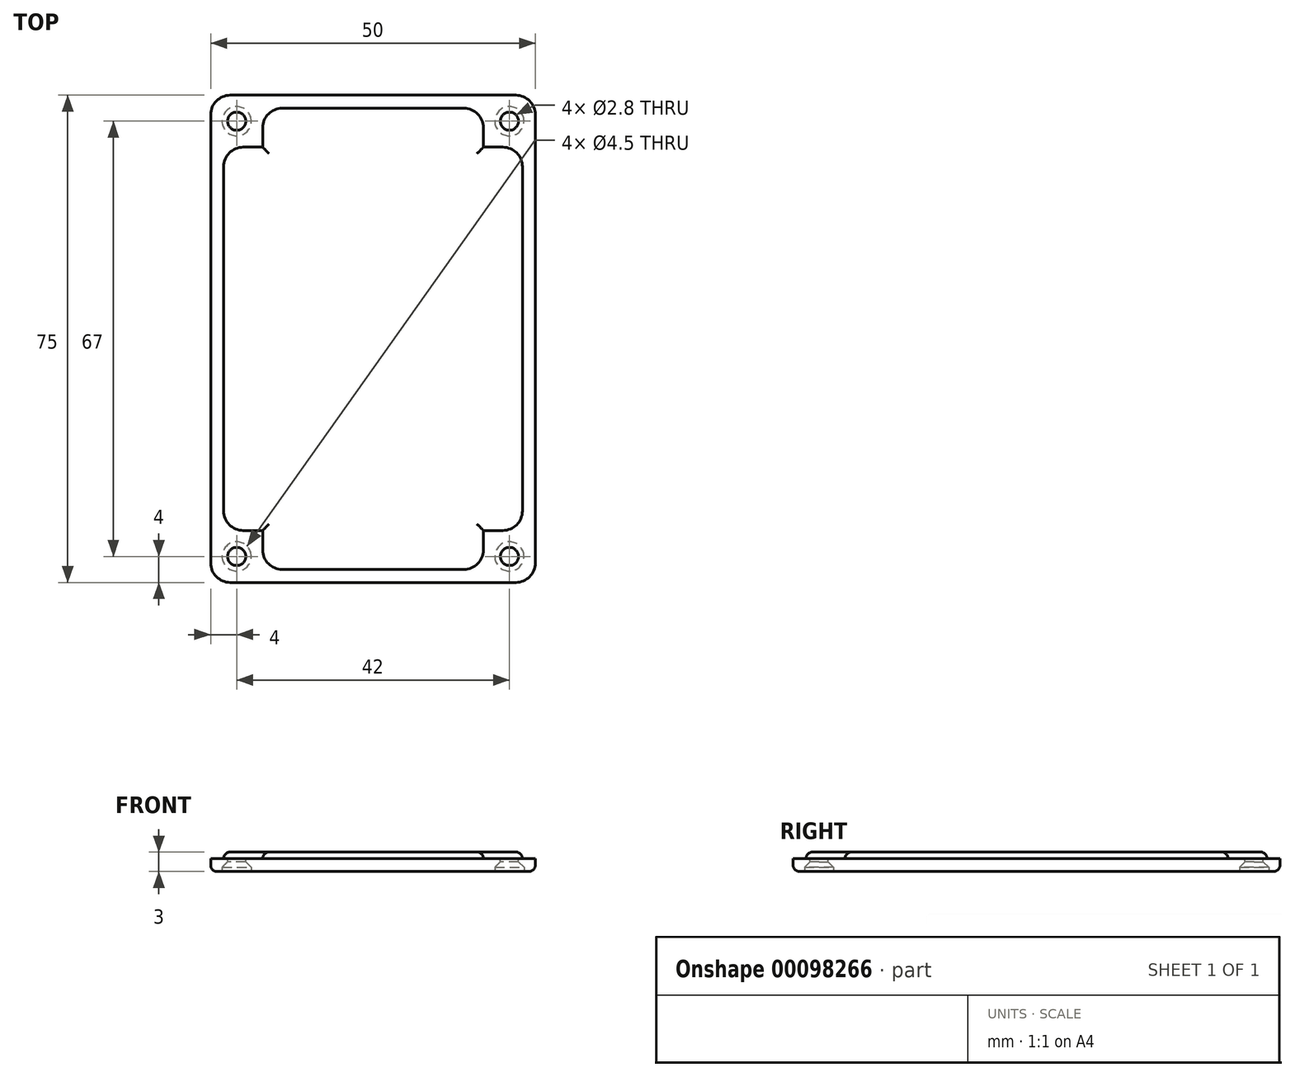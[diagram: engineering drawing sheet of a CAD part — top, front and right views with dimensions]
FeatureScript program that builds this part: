
annotation { "Feature Type Name" : "Feature", "Feature Type Description" : "" }
export const myFeature = defineFeature(function(context is Context, id is Id, definition is map)
    precondition{}
    {
        {
            var Q0;
            Q0=qCreatedBy(makeId("Top.planeOp"),FACE);
            var sketch = newSketch(context, id + "F0", { "sketchPlane" : qUnion([Q0])});
            skLineSegment(sketch, "E0.bottom", {"start": v(3, 0) * mm, "end": v(47, 0) * mm});
            skLineSegment(sketch, "E0.top", {"start": v(3, 75) * mm, "end": v(47, 75) * mm});
            skLineSegment(sketch, "E0.left", {"start": v(0, 3) * mm, "end": v(0, 72) * mm});
            skLineSegment(sketch, "E0.right", {"start": v(50, 3) * mm, "end": v(50, 72) * mm});
            skPoint(sketch, "E1.visualSharp", {"position": v(0, 75) * mm});
            skArc(sketch, "E1.filletArc", {"start": v(3, 75) * mm, "mid": v(0.88, 74.12) * mm, "end": v(0, 72) * mm});
            skPoint(sketch, "E2.visualSharp", {"position": v(50, 75) * mm});
            skArc(sketch, "E2.filletArc", {"start": v(50, 72) * mm, "mid": v(49.12, 74.12) * mm, "end": v(47, 75) * mm});
            skPoint(sketch, "E3.visualSharp", {"position": v(50, 0) * mm});
            skArc(sketch, "E3.filletArc", {"start": v(47, 0) * mm, "mid": v(49.12, 0.88) * mm, "end": v(50, 3) * mm});
            skPoint(sketch, "E4.visualSharp", {"position": v(0, 0) * mm});
            skArc(sketch, "E4.filletArc", {"start": v(0, 3) * mm, "mid": v(0.88, 0.88) * mm, "end": v(3, 0) * mm});
            skSolve(sketch);
        }
        {
            var Q0;
            Q0=makeQuery(id+"F0.imprint","IMPRINT",FACE,{"disambiguationData":[TD([[makeQuery(id+"F0.imprint","IMPRINT",EDGE,{"derivedFrom":sQuery(id+"F0.wireOp",EDGE,"E0.bottom")}),1.0]])]});
            extrude(context, id + "F1", {"entities" : qUnion([Q0]), "depth" : 2 * mm});
        }
        {
            var Q0;
            Q0=makeQuery(id+"F1.opExtrude","CAP_FACE",FACE,{"disambiguationData":[OSD([sQuery(id+"F0.wireOp",EDGE,"E0.bottom"),sQuery(id+"F0.wireOp",EDGE,"E0.top"),sQuery(id+"F0.wireOp",EDGE,"E0.left"),sQuery(id+"F0.wireOp",EDGE,"E0.right"),sQuery(id+"F0.wireOp",EDGE,"E1.filletArc"),sQuery(id+"F0.wireOp",EDGE,"E2.filletArc"),sQuery(id+"F0.wireOp",EDGE,"E3.filletArc"),sQuery(id+"F0.wireOp",EDGE,"E4.filletArc")])],"isStart":false});
            var sketch = newSketch(context, id + "F2", { "sketchPlane" : qUnion([Q0])});
            skCircle(sketch, "E5", {"center": v(4, 71) * mm, "radius": 1.4 * mm});
            skCircle(sketch, "E6", {"center": v(46, 71) * mm, "radius": 1.4 * mm});
            skCircle(sketch, "E7", {"center": v(46, 4) * mm, "radius": 1.4 * mm});
            skCircle(sketch, "E8", {"center": v(4, 4) * mm, "radius": 1.4 * mm});
            skSolve(sketch);
        }
        {
            var Q0;
            Q0=makeQuery(id+"F2.imprint","IMPRINT",FACE,{"disambiguationData":[TD([[makeQuery(id+"F2.imprint","IMPRINT",EDGE,{"derivedFrom":sQuery(id+"F2.wireOp",EDGE,"E5")}),1.0]])]});
            var Q1;
            Q1=makeQuery(id+"F2.imprint","IMPRINT",FACE,{"disambiguationData":[TD([[makeQuery(id+"F2.imprint","IMPRINT",EDGE,{"derivedFrom":sQuery(id+"F2.wireOp",EDGE,"E6")}),1.0]])]});
            var Q2;
            Q2=makeQuery(id+"F2.imprint","IMPRINT",FACE,{"disambiguationData":[TD([[makeQuery(id+"F2.imprint","IMPRINT",EDGE,{"derivedFrom":sQuery(id+"F2.wireOp",EDGE,"E8")}),1.0]])]});
            var Q3;
            Q3=makeQuery(id+"F2.imprint","IMPRINT",FACE,{"disambiguationData":[TD([[makeQuery(id+"F2.imprint","IMPRINT",EDGE,{"derivedFrom":sQuery(id+"F2.wireOp",EDGE,"E7")}),1.0]])]});
            extrude(context, id + "F3", {"entities" : qUnion([Q0, Q1, Q2, Q3]), "operationType" : NewBodyOperationType.REMOVE, "oppositeDirection" : true, "depth" : 5 * mm});
        }
        {
            var Q0;
            Q0=makeQuery(id+"F1.opExtrude","CAP_FACE",FACE,{"disambiguationData":[OSD([sQuery(id+"F0.wireOp",EDGE,"E0.bottom"),sQuery(id+"F0.wireOp",EDGE,"E0.top"),sQuery(id+"F0.wireOp",EDGE,"E0.left"),sQuery(id+"F0.wireOp",EDGE,"E0.right"),sQuery(id+"F0.wireOp",EDGE,"E1.filletArc"),sQuery(id+"F0.wireOp",EDGE,"E2.filletArc"),sQuery(id+"F0.wireOp",EDGE,"E3.filletArc"),sQuery(id+"F0.wireOp",EDGE,"E4.filletArc")])],"isStart":false});
            var sketch = newSketch(context, id + "F4", { "sketchPlane" : qUnion([Q0])});
            skLineSegment(sketch, "E9.1", {"start": v(11, 2) * mm, "end": v(39, 2) * mm});
            skLineSegment(sketch, "E9.2", {"start": v(2, 11) * mm, "end": v(2, 64) * mm});
            skLineSegment(sketch, "E9.5", {"start": v(11, 73) * mm, "end": v(39, 73) * mm});
            skLineSegment(sketch, "E9.7", {"start": v(48, 11) * mm, "end": v(48, 64) * mm});
            skLineSegment(sketch, "E10.top", {"start": v(5, 67) * mm, "end": v(8, 67) * mm});
            skLineSegment(sketch, "E10.right", {"start": v(8, 70) * mm, "end": v(8, 67) * mm});
            skLineSegment(sketch, "E11.top", {"start": v(45, 67) * mm, "end": v(42, 67) * mm});
            skLineSegment(sketch, "E11.right", {"start": v(42, 70) * mm, "end": v(42, 67) * mm});
            skLineSegment(sketch, "E12.top", {"start": v(45, 8) * mm, "end": v(42, 8) * mm});
            skLineSegment(sketch, "E12.right", {"start": v(42, 5) * mm, "end": v(42, 8) * mm});
            skLineSegment(sketch, "E13.top", {"start": v(5, 8) * mm, "end": v(8, 8) * mm});
            skLineSegment(sketch, "E13.right", {"start": v(8, 5) * mm, "end": v(8, 8) * mm});
            skPoint(sketch, "E14.visualSharp", {"position": v(2, 67) * mm});
            skArc(sketch, "E14.filletArc", {"start": v(5, 67) * mm, "mid": v(2.88, 66.12) * mm, "end": v(2, 64) * mm});
            skPoint(sketch, "E15.visualSharp", {"position": v(8, 73) * mm});
            skArc(sketch, "E15.filletArc", {"start": v(11, 73) * mm, "mid": v(8.88, 72.12) * mm, "end": v(8, 70) * mm});
            skPoint(sketch, "E16.visualSharp", {"position": v(42, 73) * mm});
            skArc(sketch, "E16.filletArc", {"start": v(42, 70) * mm, "mid": v(41.12, 72.12) * mm, "end": v(39, 73) * mm});
            skPoint(sketch, "E17.visualSharp", {"position": v(48, 67) * mm});
            skArc(sketch, "E17.filletArc", {"start": v(48, 64) * mm, "mid": v(47.12, 66.12) * mm, "end": v(45, 67) * mm});
            skPoint(sketch, "E18.visualSharp", {"position": v(48, 8) * mm});
            skArc(sketch, "E18.filletArc", {"start": v(45, 8) * mm, "mid": v(47.12, 8.88) * mm, "end": v(48, 11) * mm});
            skPoint(sketch, "E19.visualSharp", {"position": v(42, 2) * mm});
            skArc(sketch, "E19.filletArc", {"start": v(39, 2) * mm, "mid": v(41.12, 2.88) * mm, "end": v(42, 5) * mm});
            skPoint(sketch, "E20.visualSharp", {"position": v(8, 2) * mm});
            skArc(sketch, "E20.filletArc", {"start": v(8, 5) * mm, "mid": v(8.88, 2.88) * mm, "end": v(11, 2) * mm});
            skPoint(sketch, "E21.visualSharp", {"position": v(2, 8) * mm});
            skArc(sketch, "E21.filletArc", {"start": v(2, 11) * mm, "mid": v(2.88, 8.88) * mm, "end": v(5, 8) * mm});
            skSolve(sketch);
        }
        {
            var Q0;
            Q0=makeQuery(id+"F4.imprint","IMPRINT",FACE,{"disambiguationData":[TD([[makeQuery(id+"F4.imprint","IMPRINT",EDGE,{"derivedFrom":sQuery(id+"F4.wireOp",EDGE,"E9.1")}),1.0]])]});
            extrude(context, id + "F5", {"entities" : qUnion([Q0]), "operationType" : NewBodyOperationType.ADD, "depth" : 1 * mm});
        }
        {
            var Q0;
            Q0=makeQuery(id+"F5.opExtrude","CAP_EDGE",EDGE,{"disambiguationData":[OSD([sQuery(id+"F4.wireOp",EDGE,"E18.filletArc")])],"isStart":false});
            var Q1;
            Q1=makeQuery(id+"F5.opExtrude","CAP_EDGE",EDGE,{"disambiguationData":[OSD([sQuery(id+"F4.wireOp",EDGE,"E12.top")])],"isStart":false});
            var Q2;
            Q2=makeQuery(id+"F5.opExtrude","CAP_EDGE",EDGE,{"disambiguationData":[OSD([sQuery(id+"F4.wireOp",EDGE,"E12.right")])],"isStart":false});
            var Q3;
            Q3=makeQuery(id+"F5.opExtrude","CAP_EDGE",EDGE,{"disambiguationData":[OSD([sQuery(id+"F4.wireOp",EDGE,"E19.filletArc")])],"isStart":false});
            var Q4;
            Q4=makeQuery(id+"F5.opExtrude","CAP_EDGE",EDGE,{"disambiguationData":[OSD([sQuery(id+"F4.wireOp",EDGE,"E9.1")])],"isStart":false});
            var Q5;
            Q5=makeQuery(id+"F5.opExtrude","CAP_EDGE",EDGE,{"disambiguationData":[OSD([sQuery(id+"F4.wireOp",EDGE,"E20.filletArc")])],"isStart":false});
            var Q6;
            Q6=makeQuery(id+"F5.opExtrude","CAP_EDGE",EDGE,{"disambiguationData":[OSD([sQuery(id+"F4.wireOp",EDGE,"E13.right")])],"isStart":false});
            var Q7;
            Q7=makeQuery(id+"F5.opExtrude","CAP_EDGE",EDGE,{"disambiguationData":[OSD([sQuery(id+"F4.wireOp",EDGE,"E13.top")])],"isStart":false});
            var Q8;
            Q8=makeQuery(id+"F5.opExtrude","CAP_EDGE",EDGE,{"disambiguationData":[OSD([sQuery(id+"F4.wireOp",EDGE,"E21.filletArc")])],"isStart":false});
            var Q9;
            Q9=makeQuery(id+"F5.opExtrude","CAP_EDGE",EDGE,{"disambiguationData":[OSD([sQuery(id+"F4.wireOp",EDGE,"E9.2")])],"isStart":false});
            var Q10;
            Q10=makeQuery(id+"F5.opExtrude","CAP_EDGE",EDGE,{"disambiguationData":[OSD([sQuery(id+"F4.wireOp",EDGE,"E14.filletArc")])],"isStart":false});
            var Q11;
            Q11=makeQuery(id+"F5.opExtrude","CAP_EDGE",EDGE,{"disambiguationData":[OSD([sQuery(id+"F4.wireOp",EDGE,"E10.top")])],"isStart":false});
            var Q12;
            Q12=makeQuery(id+"F5.opExtrude","CAP_EDGE",EDGE,{"disambiguationData":[OSD([sQuery(id+"F4.wireOp",EDGE,"E10.right")])],"isStart":false});
            var Q13;
            Q13=makeQuery(id+"F5.opExtrude","CAP_EDGE",EDGE,{"disambiguationData":[OSD([sQuery(id+"F4.wireOp",EDGE,"E15.filletArc")])],"isStart":false});
            var Q14;
            Q14=makeQuery(id+"F5.opExtrude","CAP_EDGE",EDGE,{"disambiguationData":[OSD([sQuery(id+"F4.wireOp",EDGE,"E9.5")])],"isStart":false});
            var Q15;
            Q15=makeQuery(id+"F5.opExtrude","CAP_EDGE",EDGE,{"disambiguationData":[OSD([sQuery(id+"F4.wireOp",EDGE,"E16.filletArc")])],"isStart":false});
            var Q16;
            Q16=makeQuery(id+"F5.opExtrude","CAP_EDGE",EDGE,{"disambiguationData":[OSD([sQuery(id+"F4.wireOp",EDGE,"E11.right")])],"isStart":false});
            var Q17;
            Q17=makeQuery(id+"F5.opExtrude","CAP_EDGE",EDGE,{"disambiguationData":[OSD([sQuery(id+"F4.wireOp",EDGE,"E11.top")])],"isStart":false});
            var Q18;
            Q18=makeQuery(id+"F5.opExtrude","CAP_EDGE",EDGE,{"disambiguationData":[OSD([sQuery(id+"F4.wireOp",EDGE,"E17.filletArc")])],"isStart":false});
            var Q19;
            Q19=makeQuery(id+"F5.opExtrude","CAP_EDGE",EDGE,{"disambiguationData":[OSD([sQuery(id+"F4.wireOp",EDGE,"E9.7")])],"isStart":false});
            fillet(context, id + "F6", {"entities" : qUnion([Q0, Q1, Q2, Q3, Q4, Q5, Q6, Q7, Q8, Q9, Q10, Q11, Q12, Q13, Q14, Q15, Q16, Q17, Q18, Q19]), "radius" : 1 * mm, "tangentPropagation" : true, "allowEdgeOverflow" : false});
        }
        {
            var Q0;
            Q0=makeQuery(id+"F1.opExtrude","CAP_EDGE",EDGE,{"disambiguationData":[OSD([sQuery(id+"F0.wireOp",EDGE,"E0.left")])],"isStart":true});
            fillet(context, id + "F7", {"entities" : qUnion([Q0]), "radius" : 1 * mm, "tangentPropagation" : true, "allowEdgeOverflow" : false});
        }
        {
            var Q0;
            Q0=makeQuery(id+"F1.opExtrude","CAP_FACE",FACE,{"disambiguationData":[OSD([sQuery(id+"F0.wireOp",EDGE,"E0.bottom"),sQuery(id+"F0.wireOp",EDGE,"E0.top"),sQuery(id+"F0.wireOp",EDGE,"E0.left"),sQuery(id+"F0.wireOp",EDGE,"E0.right"),sQuery(id+"F0.wireOp",EDGE,"E1.filletArc"),sQuery(id+"F0.wireOp",EDGE,"E2.filletArc"),sQuery(id+"F0.wireOp",EDGE,"E3.filletArc"),sQuery(id+"F0.wireOp",EDGE,"E4.filletArc")])],"isStart":true});
            var sketch = newSketch(context, id + "F8", { "sketchPlane" : qUnion([Q0])});
            skCircle(sketch, "E22", {"center": v(4, -4) * mm, "radius": 2.25 * mm});
            skCircle(sketch, "E23", {"center": v(46, -4) * mm, "radius": 2.25 * mm});
            skCircle(sketch, "E24", {"center": v(46, -71) * mm, "radius": 2.25 * mm});
            skCircle(sketch, "E25", {"center": v(4, -71) * mm, "radius": 2.25 * mm});
            skSolve(sketch);
        }
        {
            var Q0;
            Q0 = qSketchRegion(id + "F8", true);
            extrude(context, id + "F9", {"entities" : qUnion([Q0]), "operationType" : NewBodyOperationType.REMOVE, "oppositeDirection" : true, "depth" : .5 * mm});
        }
        {
            var Q0;
            Q0=makeQuery(id+"F9.boolean.opBoolean","INTERSECT",EDGE,{"derivedFrom":[makeQuery(id+"F3.boolean.opBoolean","COPY",FACE,{"derivedFrom":makeQuery(id+"F3.opExtrude","SWEPT_FACE",FACE,{"disambiguationData":[OSD([sQuery(id+"F2.wireOp",EDGE,"E8")])]})}),makeQuery(id+"F9.opExtrude","CAP_FACE",FACE,{"disambiguationData":[OSD([sQuery(id+"F8.wireOp",EDGE,"E22")])],"isStart":false})]});
            var Q1;
            Q1=makeQuery(id+"F9.boolean.opBoolean","INTERSECT",EDGE,{"derivedFrom":[makeQuery(id+"F3.boolean.opBoolean","COPY",FACE,{"derivedFrom":makeQuery(id+"F3.opExtrude","SWEPT_FACE",FACE,{"disambiguationData":[OSD([sQuery(id+"F2.wireOp",EDGE,"E7")])]})}),makeQuery(id+"F9.opExtrude","CAP_FACE",FACE,{"disambiguationData":[OSD([sQuery(id+"F8.wireOp",EDGE,"E23")])],"isStart":false})]});
            var Q2;
            Q2=makeQuery(id+"F9.boolean.opBoolean","INTERSECT",EDGE,{"derivedFrom":[makeQuery(id+"F3.boolean.opBoolean","COPY",FACE,{"derivedFrom":makeQuery(id+"F3.opExtrude","SWEPT_FACE",FACE,{"disambiguationData":[OSD([sQuery(id+"F2.wireOp",EDGE,"E5")])]})}),makeQuery(id+"F9.opExtrude","CAP_FACE",FACE,{"disambiguationData":[OSD([sQuery(id+"F8.wireOp",EDGE,"E25")])],"isStart":false})]});
            var Q3;
            Q3=makeQuery(id+"F9.boolean.opBoolean","INTERSECT",EDGE,{"derivedFrom":[makeQuery(id+"F3.boolean.opBoolean","COPY",FACE,{"derivedFrom":makeQuery(id+"F3.opExtrude","SWEPT_FACE",FACE,{"disambiguationData":[OSD([sQuery(id+"F2.wireOp",EDGE,"E6")])]})}),makeQuery(id+"F9.opExtrude","CAP_FACE",FACE,{"disambiguationData":[OSD([sQuery(id+"F8.wireOp",EDGE,"E24")])],"isStart":false})]});
            chamfer(context, id + "F10", {"entities" : qUnion([Q0, Q1, Q2, Q3]), "chamferType" : ChamferType.OFFSET_ANGLE, "width" : 1 * mm, "oppositeDirection" : false, "angle" : 45 * degree, "tangentPropagation" : true});
        }
    });
